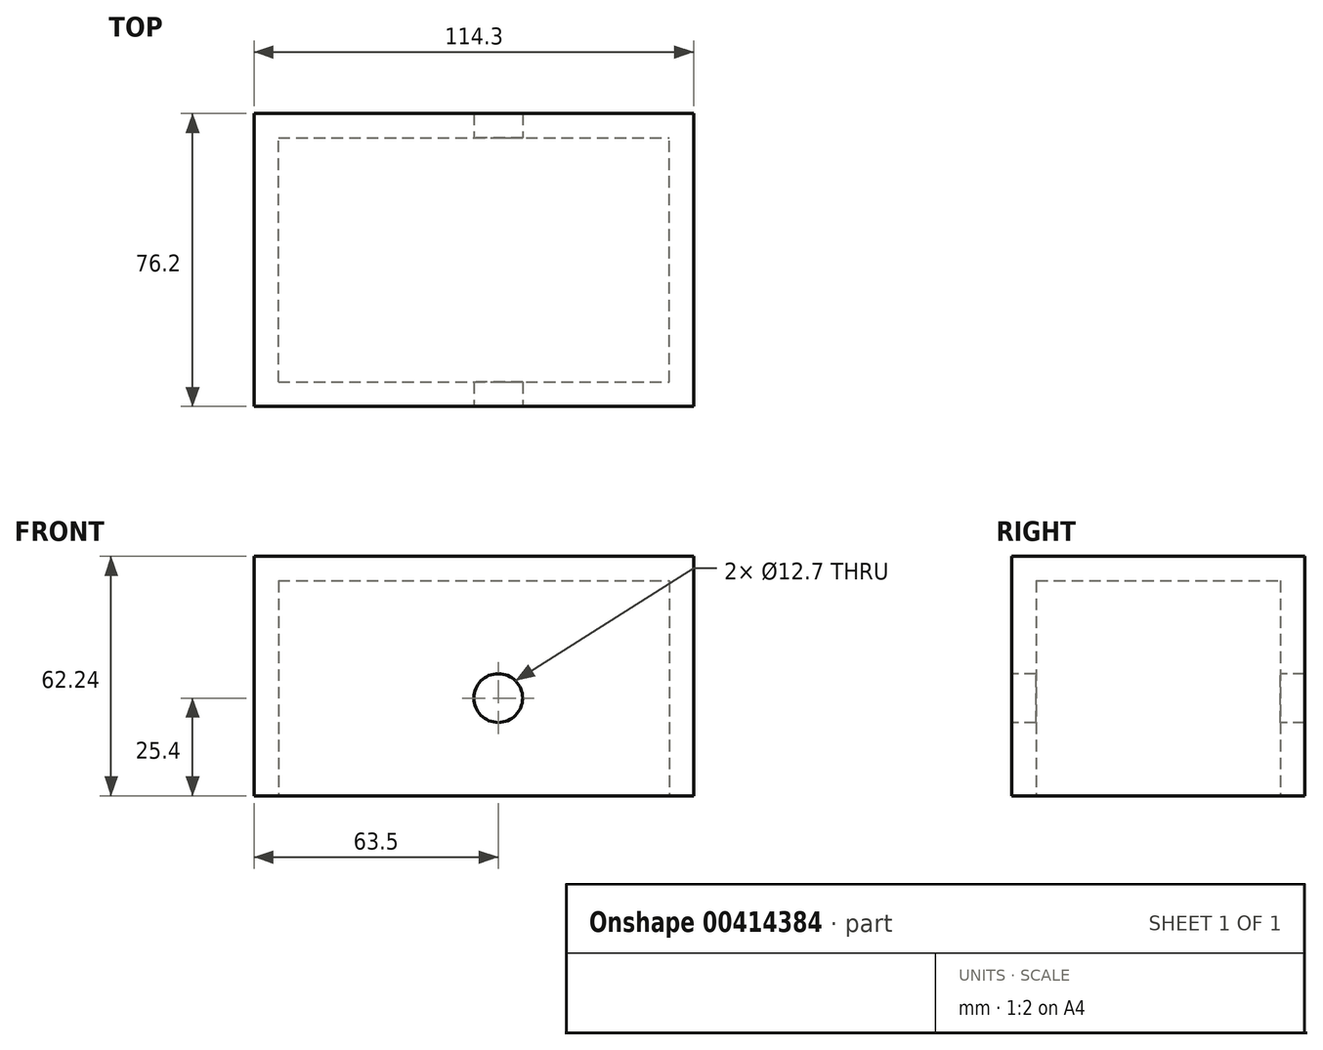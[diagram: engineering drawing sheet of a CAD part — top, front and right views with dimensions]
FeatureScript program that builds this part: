
annotation { "Feature Type Name" : "Feature", "Feature Type Description" : "" }
export const myFeature = defineFeature(function(context is Context, id is Id, definition is map)
    precondition{}
    {
        {
            var Q0;
            Q0=qCreatedBy(makeId("Front.planeOp"),FACE);
            var sketch = newSketch(context, id + "F0", { "sketchPlane" : qUnion([Q0])});
            skLineSegment(sketch, "E0.bottom", {"start": v(0, 62.24) * mm, "end": v(114.3, 62.24) * mm});
            skLineSegment(sketch, "E0.top", {"start": v(0, 0) * mm, "end": v(114.3, 0) * mm});
            skLineSegment(sketch, "E0.left", {"start": v(0, 62.24) * mm, "end": v(0, 0) * mm});
            skLineSegment(sketch, "E0.right", {"start": v(114.3, 62.24) * mm, "end": v(114.3, 0) * mm});
            skSolve(sketch);
        }
        {
            var Q0;
            Q0=makeQuery(id+"F0.imprint","IMPRINT",FACE,{"disambiguationData":[TD([[makeQuery(id+"F0.imprint","IMPRINT",EDGE,{"derivedFrom":sQuery(id+"F0.wireOp",EDGE,"E0.bottom")}),-1.0]])]});
            extrude(context, id + "F1", {"entities" : qUnion([Q0]), "endBound" : BoundingType.SYMMETRIC, "depth" : 76.2 * mm});
        }
        {
            var Q0;
            Q0=makeQuery(id+"F1.opExtrude","SWEPT_FACE",FACE,{"disambiguationData":[OSD([sQuery(id+"F0.wireOp",EDGE,"E0.top")])]});
            shell(context, id + "F2", {"entities" : qUnion([Q0]), "thickness" : 6.35 * mm});
        }
        {
            var Q0;
            Q0=makeQuery(id+"F1.opExtrude","CAP_FACE",FACE,{"disambiguationData":[OSD([sQuery(id+"F0.wireOp",EDGE,"E0.bottom"),sQuery(id+"F0.wireOp",EDGE,"E0.top"),sQuery(id+"F0.wireOp",EDGE,"E0.left"),sQuery(id+"F0.wireOp",EDGE,"E0.right")])],"isStart":false});
            var sketch = newSketch(context, id + "F3", { "sketchPlane" : qUnion([Q0])});
            skCircle(sketch, "E1", {"center": v(63.5, 25.4) * mm, "radius": 6.35 * mm});
            skSolve(sketch);
        }
        {
            var Q0;
            Q0=makeQuery(id+"F3.imprint","IMPRINT",FACE,{"disambiguationData":[TD([[makeQuery(id+"F3.imprint","IMPRINT",EDGE,{"derivedFrom":sQuery(id+"F3.wireOp",EDGE,"E1")}),1.0]])]});
            extrude(context, id + "F4", {"entities" : qUnion([Q0]), "operationType" : NewBodyOperationType.REMOVE, "endBound" : BoundingType.THROUGH_ALL, "oppositeDirection" : true, "depth" : 25.4 * mm});
        }
    });
